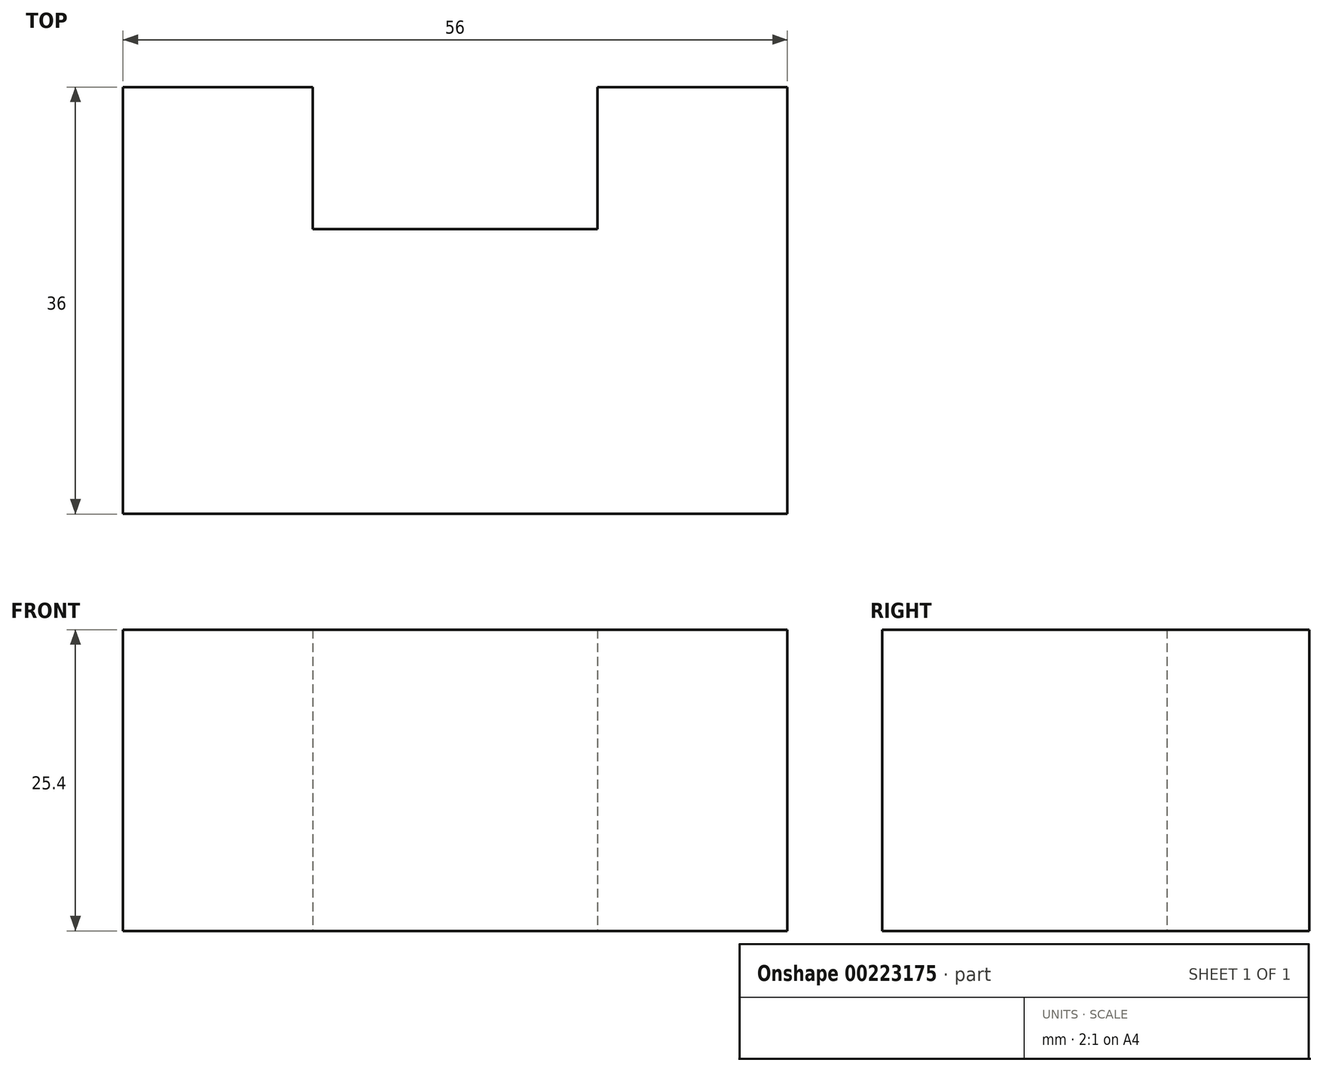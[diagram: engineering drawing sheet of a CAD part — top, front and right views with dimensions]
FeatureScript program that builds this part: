
annotation { "Feature Type Name" : "Feature", "Feature Type Description" : "" }
export const myFeature = defineFeature(function(context is Context, id is Id, definition is map)
    precondition{}
    {
        {
            var Q0;
            Q0=qCreatedBy(makeId("Top.planeOp"),FACE);
            var sketch = newSketch(context, id + "F0", { "sketchPlane" : qUnion([Q0])});
            skLineSegment(sketch, "E0.bottom", {"start": v(28, 18) * mm, "end": v(12, 18) * mm});
            skLineSegment(sketch, "E0.top", {"start": v(28, -18) * mm, "end": v(-28, -18) * mm});
            skLineSegment(sketch, "E0.left", {"start": v(28, 18) * mm, "end": v(28, -18) * mm});
            skLineSegment(sketch, "E0.right", {"start": v(-28, 18) * mm, "end": v(-28, -18) * mm});
            skPoint(sketch, "E0.middle", {"position": v(0, 0) * mm});
            skLineSegment(sketch, "E1", {"start": v(-12, 18) * mm, "end": v(-12, 6) * mm});
            skLineSegment(sketch, "E2", {"start": v(-12, 6) * mm, "end": v(12, 6) * mm});
            skLineSegment(sketch, "E3", {"start": v(12, 6) * mm, "end": v(12, 18) * mm});
            skLineSegment(sketch, "E4.trimOffspring", {"start": v(-12, 18) * mm, "end": v(-28, 18) * mm});
            skSolve(sketch);
        }
        {
            var Q0;
            Q0=makeQuery(id+"F0.imprint","IMPRINT",FACE,{"disambiguationData":[TD([[makeQuery(id+"F0.imprint","IMPRINT",EDGE,{"derivedFrom":sQuery(id+"F0.wireOp",EDGE,"E0.bottom")}),1.0]])]});
            extrude(context, id + "F1", {"entities" : qUnion([Q0]), "depth" : 25.4 * mm});
        }
    });
